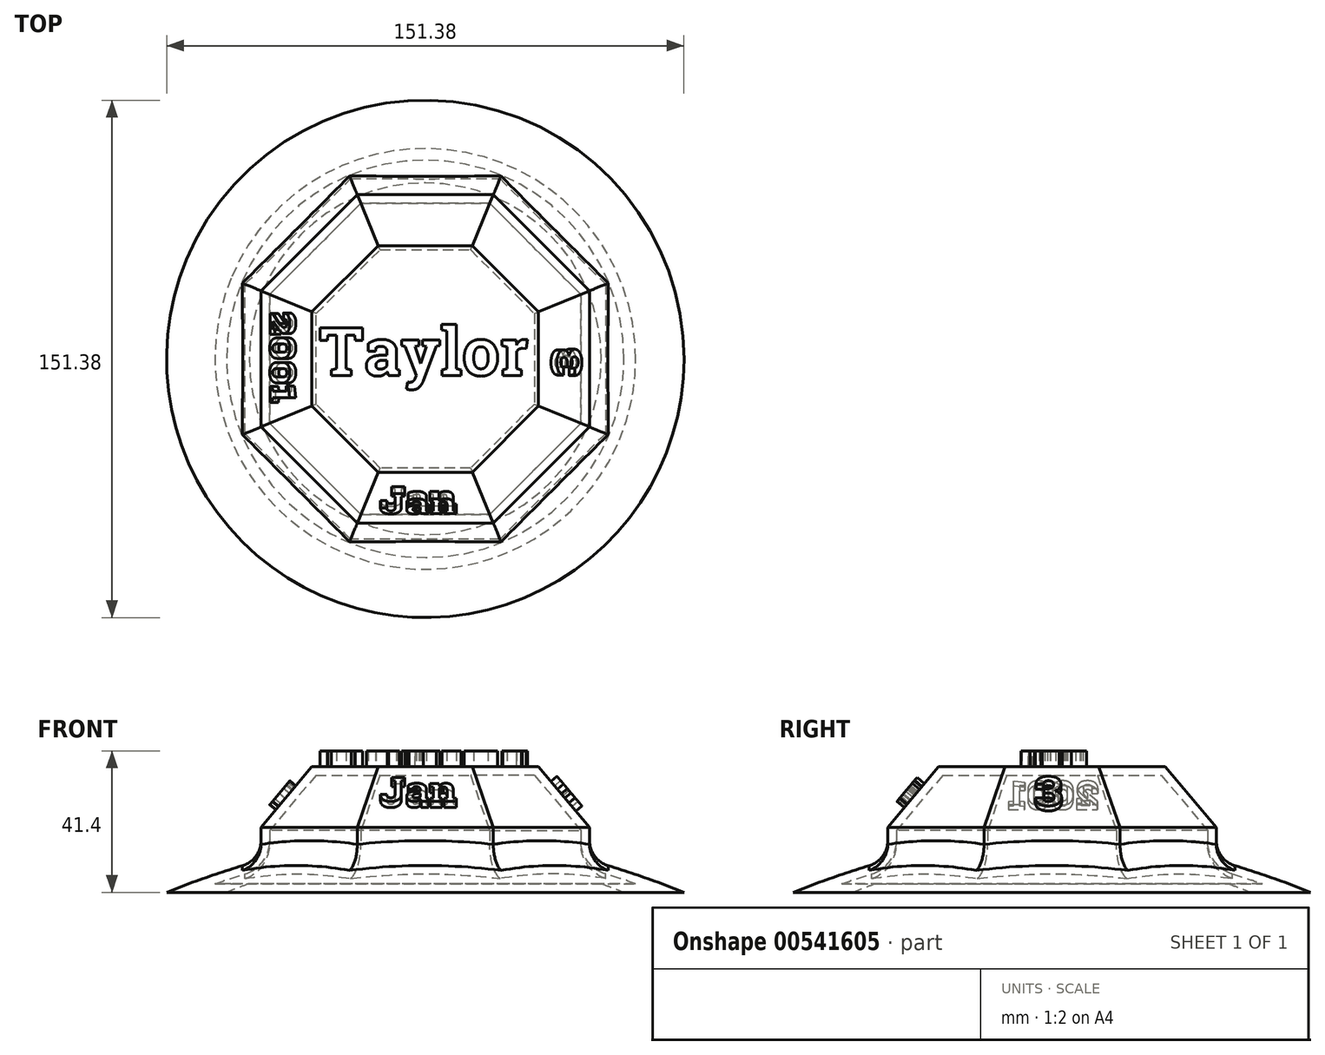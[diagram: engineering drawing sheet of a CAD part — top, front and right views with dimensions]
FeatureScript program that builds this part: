
annotation { "Feature Type Name" : "Feature", "Feature Type Description" : "" }
export const myFeature = defineFeature(function(context is Context, id is Id, definition is map)
    precondition{}
    {
        {
            var Q0;
            Q0=qCreatedBy(makeId("Front.planeOp"),FACE);
            var sketch = newSketch(context, id + "F0", { "sketchPlane" : qUnion([Q0])});
            skArc(sketch, "E0", {"start": v(0, 18.7) * mm, "mid": v(-38.5, 11.97) * mm, "end": v(-75.7, 0) * mm});
            skArc(sketch, "E1", {"start": v(0, 12.66) * mm, "mid": v(-29.6, 8.8) * mm, "end": v(-58.14, 0) * mm});
            skLineSegment(sketch, "E2", {"start": v(-58.14, 0) * mm, "end": v(-75.7, 0) * mm});
            skLineSegment(sketch, "E3", {"start": v(0, 18.7) * mm, "end": v(0, 12.66) * mm});
            skSolve(sketch);
        }
        {
            var Q0;
            Q0=makeQuery(id+"F0.imprint","IMPRINT",FACE,{"disambiguationData":[TD([[makeQuery(id+"F0.imprint","IMPRINT",EDGE,{"derivedFrom":sQuery(id+"F0.wireOp",EDGE,"E0")}),1.0]])]});
            var Q1;
            Q1=sQuery(id+"F0.wireOp",EDGE,"E3");
            revolve(context, id + "F1", {"entities" : qUnion([Q0]), "axis" : qUnion([Q1]), "revolveType" : RevolveType.FULL});
        }
        {
            var Q0;
            Q0=qCreatedBy(makeId("Top.planeOp"),FACE);
            var sketch = newSketch(context, id + "F2", { "sketchPlane" : qUnion([Q0])});
            skCircle(sketch, "E4.cCircle", {"center": v(0, 0) * mm, "radius": 48.06 * mm, "construction": true});
            skLineSegment(sketch, "E4.0", {"start": v(-19.9, 48.06) * mm, "end": v(19.9, 48.06) * mm});
            skLineSegment(sketch, "E4.1", {"start": v(19.9, 48.06) * mm, "end": v(48.06, 19.9) * mm});
            skLineSegment(sketch, "E4.2", {"start": v(48.06, 19.9) * mm, "end": v(48.06, -19.9) * mm});
            skLineSegment(sketch, "E4.3", {"start": v(48.06, -19.9) * mm, "end": v(19.9, -48.06) * mm});
            skLineSegment(sketch, "E4.4", {"start": v(19.9, -48.06) * mm, "end": v(-19.9, -48.06) * mm});
            skLineSegment(sketch, "E4.5", {"start": v(-19.9, -48.06) * mm, "end": v(-48.06, -19.9) * mm});
            skLineSegment(sketch, "E4.6", {"start": v(-48.06, -19.9) * mm, "end": v(-48.06, 19.9) * mm});
            skLineSegment(sketch, "E4.7", {"start": v(-48.06, 19.9) * mm, "end": v(-19.9, 48.06) * mm});
            skPoint(sketch, "E4.0.midPoint", {"position": v(0, 48.06) * mm});
            skSolve(sketch);
        }
        {
            var Q0;
            Q0 = qSketchRegion(id + "F2", true);
            extrude(context, id + "F3", {"entities" : qUnion([Q0]), "operationType" : NewBodyOperationType.ADD, "depth" : 19.05 * mm, "offsetDistance" : 25.4 * mm});
        }
        {
            var Q0;
            Q0=makeQuery(id+"F3.opExtrude","CAP_FACE",FACE,{"disambiguationData":[OSD([sQuery(id+"F2.wireOp",EDGE,"E4.0"),sQuery(id+"F2.wireOp",EDGE,"E4.1"),sQuery(id+"F2.wireOp",EDGE,"E4.2"),sQuery(id+"F2.wireOp",EDGE,"E4.3"),sQuery(id+"F2.wireOp",EDGE,"E4.4"),sQuery(id+"F2.wireOp",EDGE,"E4.5"),sQuery(id+"F2.wireOp",EDGE,"E4.6"),sQuery(id+"F2.wireOp",EDGE,"E4.7")])],"isStart":false});
            extrude(context, id + "F4", {"entities" : qUnion([Q0]), "operationType" : NewBodyOperationType.ADD, "depth" : 17.78 * mm, "offsetDistance" : 25.4 * mm, "hasDraft" : true, "draftAngle" : 40 * degree, "draftPullDirection" : true});
        }
        {
            var Q0;
            Q0=makeQuery(id+"F3.boolean.opBoolean","INTERSECT",EDGE,{"derivedFrom":[makeQuery(id+"F1.opRevolve","SWEPT_FACE",FACE,{"disambiguationData":[OSD([sQuery(id+"F0.wireOp",EDGE,"E0")])]}),makeQuery(id+"F3.opExtrude","SWEPT_FACE",FACE,{"disambiguationData":[OSD([sQuery(id+"F2.wireOp",EDGE,"E4.6")])]})]});
            var Q1;
            Q1=makeQuery(id+"F3.boolean.opBoolean","INTERSECT",EDGE,{"derivedFrom":[makeQuery(id+"F1.opRevolve","SWEPT_FACE",FACE,{"disambiguationData":[OSD([sQuery(id+"F0.wireOp",EDGE,"E0")])]}),makeQuery(id+"F3.opExtrude","SWEPT_FACE",FACE,{"disambiguationData":[OSD([sQuery(id+"F2.wireOp",EDGE,"E4.7")])]})]});
            var Q2;
            Q2=makeQuery(id+"F3.boolean.opBoolean","INTERSECT",EDGE,{"derivedFrom":[makeQuery(id+"F1.opRevolve","SWEPT_FACE",FACE,{"disambiguationData":[OSD([sQuery(id+"F0.wireOp",EDGE,"E0")])]}),makeQuery(id+"F3.opExtrude","SWEPT_FACE",FACE,{"disambiguationData":[OSD([sQuery(id+"F2.wireOp",EDGE,"E4.0")])]})]});
            var Q3;
            Q3=makeQuery(id+"F3.boolean.opBoolean","INTERSECT",EDGE,{"derivedFrom":[makeQuery(id+"F1.opRevolve","SWEPT_FACE",FACE,{"disambiguationData":[OSD([sQuery(id+"F0.wireOp",EDGE,"E0")])]}),makeQuery(id+"F3.opExtrude","SWEPT_FACE",FACE,{"disambiguationData":[OSD([sQuery(id+"F2.wireOp",EDGE,"E4.5")])]})]});
            var Q4;
            Q4=makeQuery(id+"F3.boolean.opBoolean","INTERSECT",EDGE,{"derivedFrom":[makeQuery(id+"F1.opRevolve","SWEPT_FACE",FACE,{"disambiguationData":[OSD([sQuery(id+"F0.wireOp",EDGE,"E0")])]}),makeQuery(id+"F3.opExtrude","SWEPT_FACE",FACE,{"disambiguationData":[OSD([sQuery(id+"F2.wireOp",EDGE,"E4.4")])]})]});
            var Q5;
            Q5=makeQuery(id+"F3.boolean.opBoolean","INTERSECT",EDGE,{"derivedFrom":[makeQuery(id+"F1.opRevolve","SWEPT_FACE",FACE,{"disambiguationData":[OSD([sQuery(id+"F0.wireOp",EDGE,"E0")])]}),makeQuery(id+"F3.opExtrude","SWEPT_FACE",FACE,{"disambiguationData":[OSD([sQuery(id+"F2.wireOp",EDGE,"E4.3")])]})]});
            var Q6;
            Q6=makeQuery(id+"F3.boolean.opBoolean","INTERSECT",EDGE,{"derivedFrom":[makeQuery(id+"F1.opRevolve","SWEPT_FACE",FACE,{"disambiguationData":[OSD([sQuery(id+"F0.wireOp",EDGE,"E0")])]}),makeQuery(id+"F3.opExtrude","SWEPT_FACE",FACE,{"disambiguationData":[OSD([sQuery(id+"F2.wireOp",EDGE,"E4.2")])]})]});
            var Q7;
            Q7=makeQuery(id+"F3.boolean.opBoolean","INTERSECT",EDGE,{"derivedFrom":[makeQuery(id+"F1.opRevolve","SWEPT_FACE",FACE,{"disambiguationData":[OSD([sQuery(id+"F0.wireOp",EDGE,"E0")])]}),makeQuery(id+"F3.opExtrude","SWEPT_FACE",FACE,{"disambiguationData":[OSD([sQuery(id+"F2.wireOp",EDGE,"E4.1")])]})]});
            fillet(context, id + "F5", {"entities" : qUnion([Q0, Q1, Q2, Q3, Q4, Q5, Q6, Q7]), "radius" : 7.62 * mm, "tangentPropagation" : true, "allowEdgeOverflow" : false});
        }
        {
            var Q0;
            Q0=qCreatedBy(makeId("Front.planeOp"),FACE);
            var sketch = newSketch(context, id + "F6", { "sketchPlane" : qUnion([Q0])});
            skArc(sketch, "E5.0", {"start": v(0, 12.66) * mm, "mid": v(-29.6, 8.8) * mm, "end": v(-58.14, 0) * mm});
            skLineSegment(sketch, "E6", {"start": v(0, 12.66) * mm, "end": v(0, 0) * mm});
            skLineSegment(sketch, "E7", {"start": v(0, 0) * mm, "end": v(-58.14, 0) * mm});
            skSolve(sketch);
        }
        {
            var Q0;
            Q0 = qSketchRegion(id + "F6", true);
            var Q1;
            Q1=sQuery(id+"F6.wireOp",EDGE,"E6");
            revolve(context, id + "F7", {"operationType" : NewBodyOperationType.REMOVE, "entities" : qUnion([Q0]), "axis" : qUnion([Q1]), "revolveType" : RevolveType.FULL, "oppositeDirection" : true});
        }
        {
            var Q0;
            Q0=makeQuery(id+"F7.boolean.opBoolean","MERGE",FACE,{"derivedFrom":[makeQuery(id+"F1.opRevolve","SWEPT_FACE",FACE,{"disambiguationData":[OSD([sQuery(id+"F0.wireOp",EDGE,"E1")])]}),makeQuery(id+"F7.opRevolve","SWEPT_FACE",FACE,{"disambiguationData":[OSD([sQuery(id+"F6.wireOp",EDGE,"E5.0")])]})]});
            shell(context, id + "F8", {"entities" : qUnion([Q0]), "thickness" : 2.54 * mm});
        }
        {
            var Q0;
            Q0=makeQuery(id+"F4.opExtrude","CAP_FACE",FACE,{"disambiguationData":[OSD([sQuery(id+"F2.wireOp",EDGE,"E4.0"),sQuery(id+"F2.wireOp",EDGE,"E4.1"),sQuery(id+"F2.wireOp",EDGE,"E4.2"),sQuery(id+"F2.wireOp",EDGE,"E4.3"),sQuery(id+"F2.wireOp",EDGE,"E4.4"),sQuery(id+"F2.wireOp",EDGE,"E4.5"),sQuery(id+"F2.wireOp",EDGE,"E4.6"),sQuery(id+"F2.wireOp",EDGE,"E4.7")])],"isStart":false});
            var sketch = newSketch(context, id + "F9", { "sketchPlane" : qUnion([Q0])});
            skText(sketch, "E8", { "text": "Taylor", "fontName": "RobotoSlab-Bold.ttf"});
            const initialGuessF9  = {"E8": [-0.0312, -0.00487, 1, 0, 0.01417]};
            skSetInitialGuess(sketch, initialGuessF9);
            skSolve(sketch);
        }
        {
            var Q0;
            Q0 = qSketchRegion(id + "F9", true);
            extrude(context, id + "F10", {"entities" : qUnion([Q0]), "operationType" : NewBodyOperationType.ADD, "depth" : 4.57 * mm, "offsetDistance" : 25.4 * mm});
        }
        {
            var Q0;
            Q0=makeQuery(id+"F4.opExtrude","SWEPT_FACE",FACE,{"disambiguationData":[OSD([sQuery(id+"F2.wireOp",EDGE,"E4.4")])]});
            var sketch = newSketch(context, id + "F11", { "sketchPlane" : qUnion([Q0])});
            skText(sketch, "E9", { "text": "Jan", "fontName": "RobotoSlab-Bold.ttf"});
            const initialGuessF11  = {"E9": [-0.0133, -0.00869, 1, 0, 0.00919]};
            skSetInitialGuess(sketch, initialGuessF11);
            skSolve(sketch);
        }
        {
            var Q0;
            Q0 = qSketchRegion(id + "F11", true);
            extrude(context, id + "F12", {"entities" : qUnion([Q0]), "operationType" : NewBodyOperationType.ADD, "depth" : 2.8 * mm, "offsetDistance" : 25.4 * mm});
        }
        {
            var Q0;
            Q0=makeQuery(id+"F4.opExtrude","SWEPT_FACE",FACE,{"disambiguationData":[OSD([sQuery(id+"F2.wireOp",EDGE,"E4.2")])]});
            var sketch = newSketch(context, id + "F13", { "sketchPlane" : qUnion([Q0])});
            skText(sketch, "E10", { "text": "3", "fontName": "RobotoSlab-Bold.ttf"});
            const initialGuessF13  = {"E10": [-0.00526, -0.00994, 1, 0, 0.01119]};
            skSetInitialGuess(sketch, initialGuessF13);
            skSolve(sketch);
        }
        {
            var Q0;
            Q0 = qSketchRegion(id + "F13", true);
            extrude(context, id + "F14", {"entities" : qUnion([Q0]), "operationType" : NewBodyOperationType.ADD, "depth" : 2.3 * mm, "offsetDistance" : 25.4 * mm});
        }
        {
            var Q0;
            Q0=makeQuery(id+"F4.opExtrude","SWEPT_FACE",FACE,{"disambiguationData":[OSD([sQuery(id+"F2.wireOp",EDGE,"E4.6")])]});
            var sketch = newSketch(context, id + "F15", { "sketchPlane" : qUnion([Q0])});
            skText(sketch, "E11", { "text": "2001", "fontName": "RobotoSlab-Bold.ttf"});
            const initialGuessF15  = {"E11": [-0.01373, -0.00952, 1, 0, 0.00906]};
            skSetInitialGuess(sketch, initialGuessF15);
            skSolve(sketch);
        }
        {
            var Q0;
            Q0 = qSketchRegion(id + "F15", true);
            extrude(context, id + "F16", {"entities" : qUnion([Q0]), "operationType" : NewBodyOperationType.ADD, "depth" : 2.3 * mm, "offsetDistance" : 25.4 * mm});
        }
    });
